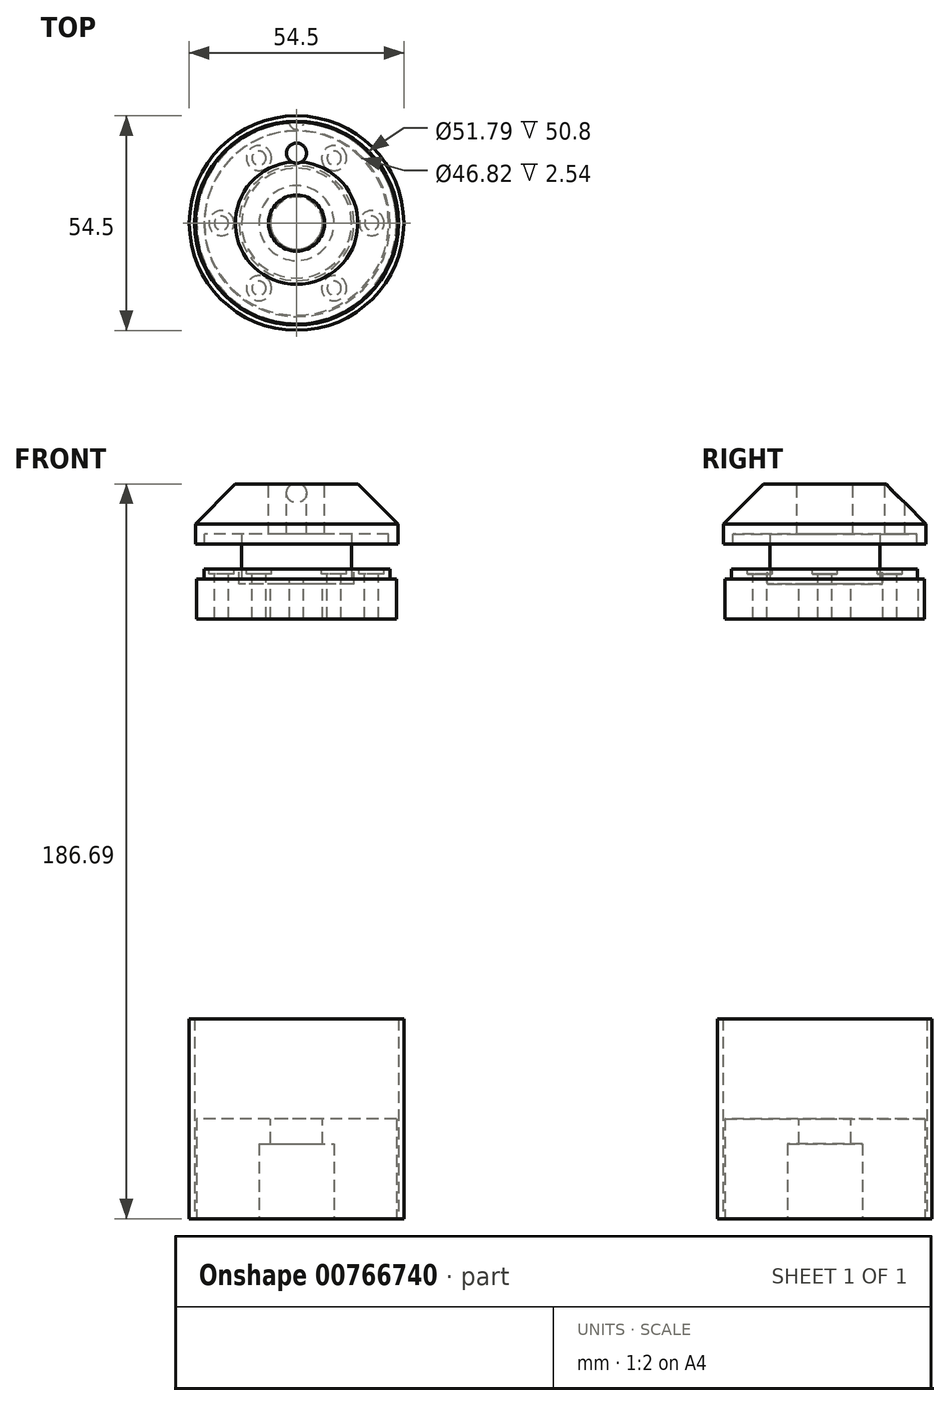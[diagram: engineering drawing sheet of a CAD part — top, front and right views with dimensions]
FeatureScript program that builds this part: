
annotation { "Feature Type Name" : "Feature", "Feature Type Description" : "" }
export const myFeature = defineFeature(function(context is Context, id is Id, definition is map)
    precondition{}
    {
        {
            var Q0;
            Q0=qCreatedBy(makeId("Top.planeOp"),FACE);
            var sketch = newSketch(context, id + "F0", { "sketchPlane" : qUnion([Q0])});
            skCircle(sketch, "E0", {"center": v(0, 0) * mm, "radius": 25.4 * mm});
            skSolve(sketch);
        }
        {
            var Q0;
            Q0 = qSketchRegion(id + "F0", true);
            extrude(context, id + "F1", {"entities" : qUnion([Q0]), "depth" : 25.4 * mm, "offsetDistance" : 25.4 * mm});
        }
        {
            var Q0;
            Q0=makeQuery(id+"F1.opExtrude","CAP_FACE",FACE,{"disambiguationData":[OSD([sQuery(id+"F0.wireOp",EDGE,"E0")])],"isStart":false});
            var sketch = newSketch(context, id + "F2", { "sketchPlane" : qUnion([Q0])});
            skCircle(sketch, "E1", {"center": v(0, 0) * mm, "radius": 6.6 * mm});
            skSolve(sketch);
        }
        {
            var Q0;
            Q0 = qSketchRegion(id + "F2", true);
            extrude(context, id + "F3", {"entities" : qUnion([Q0]), "operationType" : NewBodyOperationType.REMOVE, "endBound" : BoundingType.THROUGH_ALL, "oppositeDirection" : true, "depth" : 25.4 * mm, "offsetDistance" : 25.4 * mm});
        }
        {
            var Q0;
            Q0=makeQuery(id+"F1.opExtrude","CAP_FACE",FACE,{"disambiguationData":[OSD([sQuery(id+"F0.wireOp",EDGE,"E0")])],"isStart":true});
            var sketch = newSketch(context, id + "F4", { "sketchPlane" : qUnion([Q0])});
            skCircle(sketch, "E2", {"center": v(0, 0) * mm, "radius": 9.53 * mm});
            skSolve(sketch);
        }
        {
            var Q0;
            Q0 = qSketchRegion(id + "F4", true);
            extrude(context, id + "F5", {"entities" : qUnion([Q0]), "operationType" : NewBodyOperationType.REMOVE, "oppositeDirection" : true, "depth" : 19.05 * mm, "offsetDistance" : 25.4 * mm});
        }
        {
            var Q0;
            Q0=makeQuery(id+"F1.opExtrude","CAP_FACE",FACE,{"disambiguationData":[OSD([sQuery(id+"F0.wireOp",EDGE,"E0")])],"isStart":false});
            var sketch = newSketch(context, id + "F6", { "sketchPlane" : qUnion([Q0])});
            skCircle(sketch, "E3.0", {"center": v(0, 0) * mm, "radius": 12.7 * mm});
            skSolve(sketch);
        }
        {
            var Q0;
            Q0=makeQuery(id+"F6.imprint","IMPRINT",FACE,{"disambiguationData":[TD([[makeQuery(id+"F6.imprint","IMPRINT",EDGE,{"derivedFrom":sQuery(id+"F6.wireOp",EDGE,"E3.0")}),1.0]])]});
            var sketch = newSketch(context, id + "F7", { "sketchPlane" : qUnion([Q0])});
            skCircle(sketch, "E4", {"center": v(-11.5, 0) * mm, "radius": 3.18 * mm});
            skCircle(sketch, "E5.1.0", {"center": v(-5.75, -9.97) * mm, "radius": 3.18 * mm});
            skCircle(sketch, "E5.2.0", {"center": v(5.75, -9.97) * mm, "radius": 3.18 * mm});
            skCircle(sketch, "E5.3.0", {"center": v(11.5, 0) * mm, "radius": 3.18 * mm});
            skCircle(sketch, "E5.4.0", {"center": v(5.75, 9.97) * mm, "radius": 3.18 * mm});
            skCircle(sketch, "E5.5.0", {"center": v(-5.75, 9.97) * mm, "radius": 3.18 * mm});
            skPoint(sketch, "E5.center", {"position": v(0, 0) * mm});
            skSolve(sketch);
        }
        {
            var Q0;
            Q0=sQuery(id+"F7.wireOp",EDGE,"E4");
            var Q1;
            Q1=sQuery(id+"F7.wireOp",EDGE,"E5.5.0");
            var Q2;
            Q2=sQuery(id+"F7.wireOp",EDGE,"E5.4.0");
            var Q3;
            Q3=sQuery(id+"F7.wireOp",EDGE,"E5.3.0");
            var Q4;
            Q4=sQuery(id+"F7.wireOp",EDGE,"E5.2.0");
            var Q5;
            Q5=sQuery(id+"F7.wireOp",EDGE,"E5.1.0");
            extrude(context, id + "F8", {"bodyType" : ToolBodyType.SURFACE, "surfaceEntities" : qUnion([Q0, Q1, Q2, Q3, Q4, Q5]), "depth" : 127 * mm, "offsetDistance" : 25.4 * mm});
        }
        {
            var Q0;
            Q0=makeQuery(id+"F6.imprint","IMPRINT",FACE,{"disambiguationData":[TD([[makeQuery(id+"F6.imprint","IMPRINT",EDGE,{"derivedFrom":sQuery(id+"F6.wireOp",EDGE,"E3.0")}),-1.0]])]});
            var sketch = newSketch(context, id + "F9", { "sketchPlane" : qUnion([Q0])});
            skCircle(sketch, "E6", {"center": v(0.15, -0.15) * mm, "radius": 25.4 * mm});
            skSolve(sketch);
        }
        {
            var Q0;
            Q0=qCreatedBy(makeId("Top.planeOp"),FACE);
            cPlane(context, id + "F10", {"entities" : qUnion([Q0]), "cplaneType" : CPlaneType.OFFSET, "offset" : 152.4 * mm, "width" : 152.4 * mm, "height" : 152.4 * mm});
        }
        {
            var Q0;
            Q0=qCreatedBy(id+"F10.planeOp",FACE);
            var sketch = newSketch(context, id + "F11", { "sketchPlane" : qUnion([Q0])});
            skCircle(sketch, "E7", {"center": v(0, 0) * mm, "radius": 25.4 * mm});
            skSolve(sketch);
        }
        {
            var Q0;
            Q0 = qSketchRegion(id + "F11", true);
            extrude(context, id + "F12", {"entities" : qUnion([Q0]), "depth" : 12.7 * mm, "offsetDistance" : 25.4 * mm});
        }
        {
            var Q0;
            Q0=makeQuery(id+"F12.opExtrude","CAP_FACE",FACE,{"disambiguationData":[OSD([sQuery(id+"F11.wireOp",EDGE,"E7")])],"isStart":false});
            var sketch = newSketch(context, id + "F13", { "sketchPlane" : qUnion([Q0])});
            skCircle(sketch, "E8", {"center": v(0, 0) * mm, "radius": 6.6 * mm});
            skSolve(sketch);
        }
        {
            var Q0;
            Q0 = qSketchRegion(id + "F13", true);
            extrude(context, id + "F14", {"entities" : qUnion([Q0]), "operationType" : NewBodyOperationType.REMOVE, "endBound" : BoundingType.THROUGH_ALL, "oppositeDirection" : true, "depth" : 25.4 * mm, "offsetDistance" : 25.4 * mm});
        }
        {
            var Q0;
            Q0=makeQuery(id+"F12.opExtrude","CAP_FACE",FACE,{"disambiguationData":[OSD([sQuery(id+"F11.wireOp",EDGE,"E7")])],"isStart":false});
            var sketch = newSketch(context, id + "F15", { "sketchPlane" : qUnion([Q0])});
            skCircle(sketch, "E9", {"center": v(-9.55, 16.54) * mm, "radius": 3.18 * mm});
            skCircle(sketch, "E10.1.0", {"center": v(-19.1, 0) * mm, "radius": 3.18 * mm});
            skCircle(sketch, "E10.2.0", {"center": v(-9.55, -16.54) * mm, "radius": 3.18 * mm});
            skCircle(sketch, "E10.3.0", {"center": v(9.55, -16.54) * mm, "radius": 3.18 * mm});
            skCircle(sketch, "E10.4.0", {"center": v(19.1, 0) * mm, "radius": 3.18 * mm});
            skCircle(sketch, "E10.5.0", {"center": v(9.55, 16.54) * mm, "radius": 3.18 * mm});
            skPoint(sketch, "E10.center", {"position": v(0, 0) * mm});
            skSolve(sketch);
        }
        {
            var Q0;
            Q0 = qSketchRegion(id + "F15", true);
            extrude(context, id + "F16", {"entities" : qUnion([Q0]), "operationType" : NewBodyOperationType.REMOVE, "oppositeDirection" : true, "depth" : 1.27 * mm, "offsetDistance" : 25.4 * mm});
        }
        {
            var Q0;
            Q0=makeQuery(id+"F16.boolean.opBoolean","COPY",FACE,{"derivedFrom":makeQuery(id+"F16.opExtrude","CAP_FACE",FACE,{"disambiguationData":[OSD([sQuery(id+"F15.wireOp",EDGE,"E10.1.0")])],"isStart":false})});
            var sketch = newSketch(context, id + "F17", { "sketchPlane" : qUnion([Q0])});
            skCircle(sketch, "E11", {"center": v(-19.1, 0) * mm, "radius": 1.78 * mm});
            skCircle(sketch, "E12", {"center": v(-9.55, 16.54) * mm, "radius": 1.78 * mm});
            skCircle(sketch, "E13", {"center": v(9.55, 16.54) * mm, "radius": 1.78 * mm});
            skCircle(sketch, "E14", {"center": v(19.1, 0) * mm, "radius": 1.78 * mm});
            skCircle(sketch, "E15", {"center": v(9.55, -16.54) * mm, "radius": 1.78 * mm});
            skCircle(sketch, "E16", {"center": v(-9.55, -16.54) * mm, "radius": 1.78 * mm});
            skSolve(sketch);
        }
        {
            var Q0;
            Q0 = qSketchRegion(id + "F17", true);
            extrude(context, id + "F18", {"entities" : qUnion([Q0]), "operationType" : NewBodyOperationType.REMOVE, "oppositeDirection" : true, "depth" : 12.7 * mm, "offsetDistance" : 25.4 * mm});
        }
        {
            var Q0;
            Q0=makeQuery(id+"F12.opExtrude","CAP_FACE",FACE,{"disambiguationData":[OSD([sQuery(id+"F11.wireOp",EDGE,"E7")])],"isStart":false});
            var sketch = newSketch(context, id + "F19", { "sketchPlane" : qUnion([Q0])});
            skCircle(sketch, "E17", {"center": v(0, 0) * mm, "radius": 14.6 * mm});
            skSolve(sketch);
        }
        {
            var Q0;
            Q0 = qSketchRegion(id + "F19", true);
            extrude(context, id + "F20", {"entities" : qUnion([Q0]), "operationType" : NewBodyOperationType.REMOVE, "oppositeDirection" : true, "depth" : 3.8 * mm, "offsetDistance" : 25.4 * mm});
        }
        {
            var Q0;
            Q0=makeQuery(id+"F12.opExtrude","CAP_FACE",FACE,{"disambiguationData":[OSD([sQuery(id+"F11.wireOp",EDGE,"E7")])],"isStart":false});
            var sketch = newSketch(context, id + "F21", { "sketchPlane" : qUnion([Q0])});
            skCircle(sketch, "E18.0", {"center": v(0.15, -0.15) * mm, "radius": 23.62 * mm});
            skCircle(sketch, "E19.0", {"center": v(0.15, -0.15) * mm, "radius": 29.97 * mm});
            skSolve(sketch);
        }
        {
            var Q0;
            Q0=makeQuery(id+"F21.imprint","IMPRINT",FACE,{"disambiguationData":[TD([[makeQuery(id+"F21.imprint","IMPRINT",EDGE,{"derivedFrom":sQuery(id+"F21.wireOp",EDGE,"E19.0")}),1.0]])]});
            var Q1;
            Q1=makeQuery(id+"F21.imprint","IMPRINT",FACE,{"disambiguationData":[TD([[makeQuery(id+"F21.imprint","IMPRINT",EDGE,{"derivedFrom":sQuery(id+"F21.wireOp",EDGE,"E18.0")}),-1.0]])]});
            var Q2;
            Q2 = qConstructionFilter(qBodyType(qCreatedBy(id + "F21" ,EDGE), BodyType.WIRE), ConstructionObject.NO);
            extrude(context, id + "F22", {"entities" : qUnion([Q0, Q1]), "operationType" : NewBodyOperationType.REMOVE, "surfaceEntities" : qUnion([Q2]), "oppositeDirection" : true, "depth" : 2.54 * mm, "offsetDistance" : 25.4 * mm});
        }
        {
            var Q0;
            Q0=makeQuery(id+"F20.boolean.opBoolean","COPY",FACE,{"derivedFrom":makeQuery(id+"F20.opExtrude","CAP_FACE",FACE,{"disambiguationData":[OSD([sQuery(id+"F19.wireOp",EDGE,"E17")])],"isStart":false})});
            var sketch = newSketch(context, id + "F23", { "sketchPlane" : qUnion([Q0])});
            skCircle(sketch, "E20", {"center": v(0, 0) * mm, "radius": 13.97 * mm});
            skSolve(sketch);
        }
        {
            var Q0;
            Q0 = qSketchRegion(id + "F23", true);
            extrude(context, id + "F24", {"entities" : qUnion([Q0]), "operationType" : NewBodyOperationType.ADD, "depth" : 12.7 * mm, "offsetDistance" : 25.4 * mm});
        }
        {
            var Q0;
            Q0=makeQuery(id+"F24.opExtrude","CAP_FACE",FACE,{"disambiguationData":[OSD([sQuery(id+"F23.wireOp",EDGE,"E20")])],"isStart":false});
            var sketch = newSketch(context, id + "F25", { "sketchPlane" : qUnion([Q0])});
            skCircle(sketch, "E21", {"center": v(0, 0) * mm, "radius": 23.5 * mm});
            skSolve(sketch);
        }
        {
            var Q0;
            Q0 = qSketchRegion(id + "F25", true);
            extrude(context, id + "F26", {"entities" : qUnion([Q0]), "operationType" : NewBodyOperationType.ADD, "depth" : 12.7 * mm, "offsetDistance" : 25.4 * mm});
        }
        {
            var Q0;
            Q0=makeQuery(id+"F26.opExtrude","CAP_FACE",FACE,{"disambiguationData":[OSD([sQuery(id+"F25.wireOp",EDGE,"E21")])],"isStart":false});
            var sketch = newSketch(context, id + "F27", { "sketchPlane" : qUnion([Q0])});
            skCircle(sketch, "E22", {"center": v(0, 0) * mm, "radius": 7.11 * mm});
            skSolve(sketch);
        }
        {
            var Q0;
            Q0 = qSketchRegion(id + "F27", true);
            extrude(context, id + "F28", {"entities" : qUnion([Q0]), "operationType" : NewBodyOperationType.REMOVE, "oppositeDirection" : true, "depth" : 12.7 * mm, "offsetDistance" : 25.4 * mm});
        }
        {
            var Q0;
            Q0=qCreatedBy(id+"F10.planeOp",FACE);
            cPlane(context, id + "F29", {"entities" : qUnion([Q0]), "cplaneType" : CPlaneType.OFFSET, "offset" : 35.56 * mm, "width" : 152.4 * mm, "height" : 152.4 * mm});
        }
        {
            var Q0;
            Q0=qCreatedBy(id+"F29.planeOp",FACE);
            var sketch = newSketch(context, id + "F30", { "sketchPlane" : qUnion([Q0])});
            skCircle(sketch, "E23", {"center": v(0, 25.63) * mm, "radius": 1.84 * mm});
            skSolve(sketch);
        }
        {
            var Q0;
            Q0 = qSketchRegion(id + "F30", true);
            extrude(context, id + "F31", {"entities" : qUnion([Q0]), "operationType" : NewBodyOperationType.REMOVE, "oppositeDirection" : true, "depth" : 50.8 * mm, "offsetDistance" : 25.4 * mm});
        }
        {
            var Q0;
            Q0=makeQuery(id+"F26.opExtrude","CAP_FACE",FACE,{"disambiguationData":[OSD([sQuery(id+"F25.wireOp",EDGE,"E21")])],"isStart":false});
            var sketch = newSketch(context, id + "F32", { "sketchPlane" : qUnion([Q0])});
            skCircle(sketch, "E24", {"center": v(0, 0) * mm, "radius": 25.72 * mm});
            skCircle(sketch, "E25", {"center": v(0, 0) * mm, "radius": 23.41 * mm});
            skSolve(sketch);
        }
        {
            var Q0;
            Q0 = qSketchRegion(id + "F32", true);
            extrude(context, id + "F33", {"entities" : qUnion([Q0]), "operationType" : NewBodyOperationType.ADD, "oppositeDirection" : true, "depth" : 15.24 * mm, "offsetDistance" : 25.4 * mm});
        }
        {
            var Q0;
            Q0=makeQuery(id+"F33.boolean.opBoolean","MERGE",FACE,{"derivedFrom":[makeQuery(id+"F26.opExtrude","CAP_FACE",FACE,{"disambiguationData":[OSD([sQuery(id+"F25.wireOp",EDGE,"E21")])],"isStart":false}),makeQuery(id+"F33.opExtrude","CAP_FACE",FACE,{"disambiguationData":[OSD([sQuery(id+"F32.wireOp",EDGE,"E24"),sQuery(id+"F32.wireOp",EDGE,"E25")])],"isStart":true})]});
            var sketch = newSketch(context, id + "F34", { "sketchPlane" : qUnion([Q0])});
            skCircle(sketch, "E26", {"center": v(0, 0) * mm, "radius": 17.78 * mm});
            skCircle(sketch, "E27", {"center": v(0, 17.78) * mm, "radius": 2.54 * mm});
            skSolve(sketch);
        }
        {
            var Q0;
            Q0=makeQuery(id+"F34.imprint","IMPRINT",FACE,{"disambiguationData":[TD([[makeQuery(id+"F34.imprint","IMPRINT",EDGE,{"derivedFrom":sQuery(id+"F34.wireOp",EDGE,"E27")}),1.0]])]});
            extrude(context, id + "F35", {"entities" : qUnion([Q0]), "operationType" : NewBodyOperationType.REMOVE, "endBound" : BoundingType.UP_TO_NEXT, "oppositeDirection" : true, "depth" : 12.7 * mm, "offsetDistance" : 25.4 * mm});
        }
        {
            var Q0;
            Q0=makeQuery(id+"F33.opExtrude","CAP_EDGE",EDGE,{"disambiguationData":[OSD([sQuery(id+"F32.wireOp",EDGE,"E24")])],"isStart":true});
            chamfer(context, id + "F36", {"entities" : qUnion([Q0]), "width" : 10.16 * mm, "tangentPropagation" : true});
        }
        {
            var Q0;
            Q0=makeQuery(id+"F1.opExtrude","CAP_FACE",FACE,{"disambiguationData":[OSD([sQuery(id+"F0.wireOp",EDGE,"E0")])],"isStart":true});
            var sketch = newSketch(context, id + "F37", { "sketchPlane" : qUnion([Q0])});
            skCircle(sketch, "E28", {"center": v(0, 0) * mm, "radius": 25.9 * mm});
            skCircle(sketch, "E29", {"center": v(0, 0) * mm, "radius": 27.25 * mm});
            skSolve(sketch);
        }
        {
            var Q0;
            Q0 = qSketchRegion(id + "F37", true);
            extrude(context, id + "F38", {"entities" : qUnion([Q0]), "oppositeDirection" : true, "depth" : 50.8 * mm, "offsetDistance" : 25.4 * mm});
        }
    });
